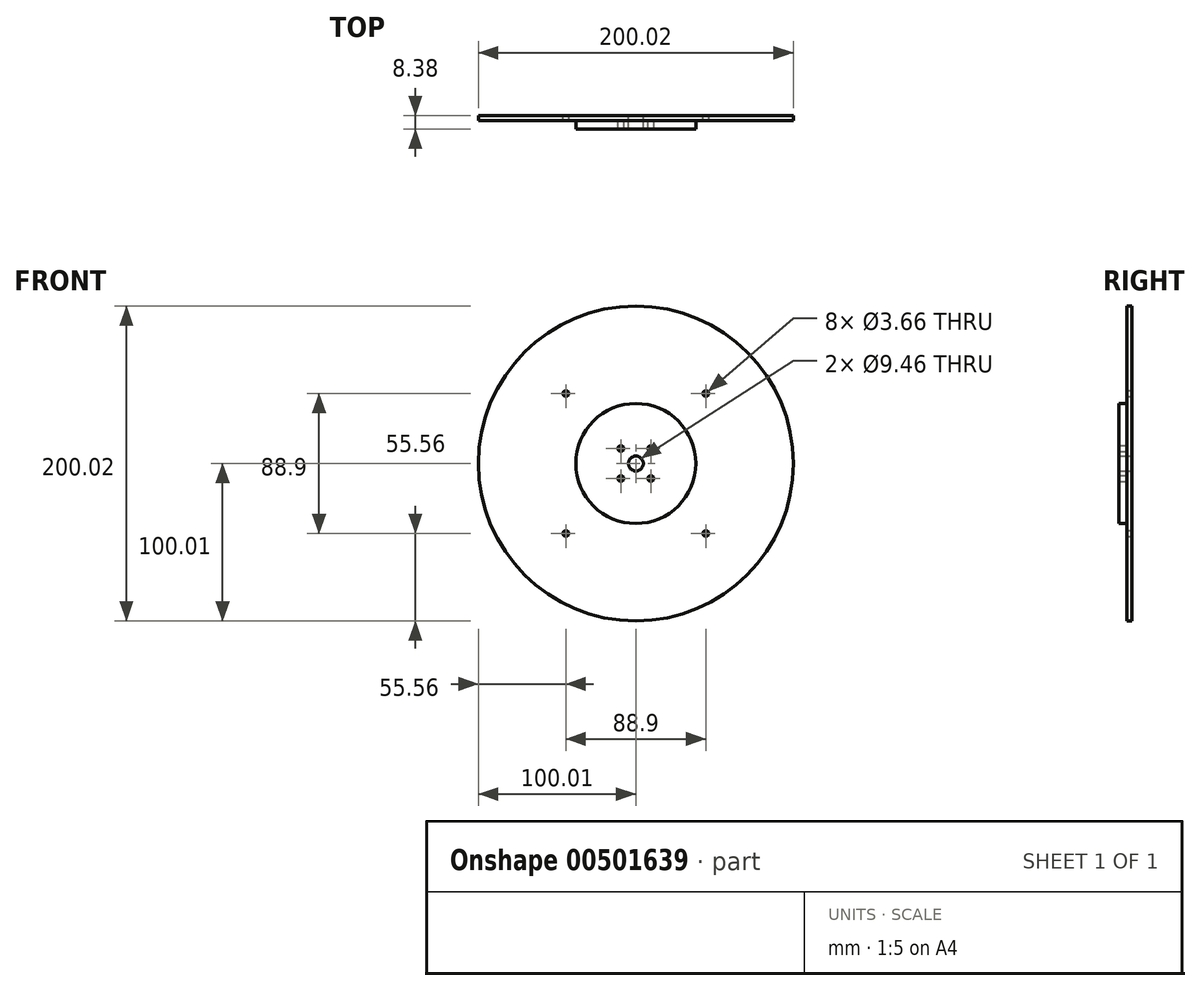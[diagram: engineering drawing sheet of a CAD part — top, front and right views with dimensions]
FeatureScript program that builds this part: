
annotation { "Feature Type Name" : "Feature", "Feature Type Description" : "" }
export const myFeature = defineFeature(function(context is Context, id is Id, definition is map)
    precondition{}
    {
        {
            var Q0;
            Q0=qCreatedBy(makeId("Front.planeOp"),FACE);
            var sketch = newSketch(context, id + "F0", { "sketchPlane" : qUnion([Q0])});
            skLineSegment(sketch, "E0.bottom", {"start": v(-44.45, 44.45) * mm, "end": v(44.45, 44.45) * mm, "construction": true});
            skLineSegment(sketch, "E0.top", {"start": v(-44.45, -44.45) * mm, "end": v(44.45, -44.45) * mm, "construction": true});
            skLineSegment(sketch, "E0.left", {"start": v(-44.45, 44.45) * mm, "end": v(-44.45, -44.45) * mm, "construction": true});
            skLineSegment(sketch, "E0.right", {"start": v(44.45, 44.45) * mm, "end": v(44.45, -44.45) * mm, "construction": true});
            skCircle(sketch, "E1", {"center": v(44.45, -44.45) * mm, "radius": 1.83 * mm});
            skCircle(sketch, "E2", {"center": v(44.45, 44.45) * mm, "radius": 1.83 * mm});
            skCircle(sketch, "E3", {"center": v(-44.45, 44.45) * mm, "radius": 1.83 * mm});
            skCircle(sketch, "E4", {"center": v(-44.45, -44.45) * mm, "radius": 1.83 * mm});
            skCircle(sketch, "E5", {"center": v(0, 0) * mm, "radius": 100.01 * mm});
            skCircle(sketch, "E6", {"center": v(0, 0) * mm, "radius": 4.73 * mm});
            skSolve(sketch);
        }
        {
            var Q0;
            Q0=qSketchRegion(id+"F0",true);
            extrude(context, id + "F1", {"entities" : qUnion([Q0]), "depth" : 3.17 * mm});
        }
        {
            var Q0;
            Q0=makeQuery(id+"F1.opExtrude","CAP_FACE",FACE,{"disambiguationData":[OSD([sQuery(id+"F0.wireOp",EDGE,"E1"),sQuery(id+"F0.wireOp",EDGE,"E2"),sQuery(id+"F0.wireOp",EDGE,"E3"),sQuery(id+"F0.wireOp",EDGE,"E4"),sQuery(id+"F0.wireOp",EDGE,"E5"),sQuery(id+"F0.wireOp",EDGE,"E6")])],"isStart":false});
            var sketch = newSketch(context, id + "F2", { "sketchPlane" : qUnion([Q0])});
            skCircle(sketch, "E7.0", {"center": v(0, 0) * mm, "radius": 4.73 * mm});
            skCircle(sketch, "E8", {"center": v(0, 0) * mm, "radius": 38.1 * mm});
            skLineSegment(sketch, "E9.bottom", {"start": v(-9.53, 9.52) * mm, "end": v(9.52, 9.53) * mm, "construction": true});
            skLineSegment(sketch, "E9.top", {"start": v(-9.53, -9.52) * mm, "end": v(9.52, -9.52) * mm, "construction": true});
            skLineSegment(sketch, "E9.left", {"start": v(-9.53, 9.52) * mm, "end": v(-9.53, -9.53) * mm, "construction": true});
            skLineSegment(sketch, "E9.right", {"start": v(9.52, 9.53) * mm, "end": v(9.52, -9.52) * mm, "construction": true});
            skCircle(sketch, "E10", {"center": v(9.52, 9.53) * mm, "radius": 1.83 * mm});
            skCircle(sketch, "E11", {"center": v(-9.53, 9.52) * mm, "radius": 1.83 * mm});
            skCircle(sketch, "E12", {"center": v(-9.53, -9.52) * mm, "radius": 1.83 * mm});
            skCircle(sketch, "E13", {"center": v(9.52, -9.52) * mm, "radius": 1.83 * mm});
            skSolve(sketch);
        }
        {
            var Q0;
            Q0=makeQuery(id+"F2.imprint","IMPRINT",FACE,{"disambiguationData":[TD([[makeQuery(id+"F2.imprint","IMPRINT",EDGE,{"derivedFrom":sQuery(id+"F2.wireOp",EDGE,"E7.0")}),-1.0]])]});
            extrude(context, id + "F3", {"entities" : qUnion([Q0]), "depth" : 5.2 * mm});
        }
    });
